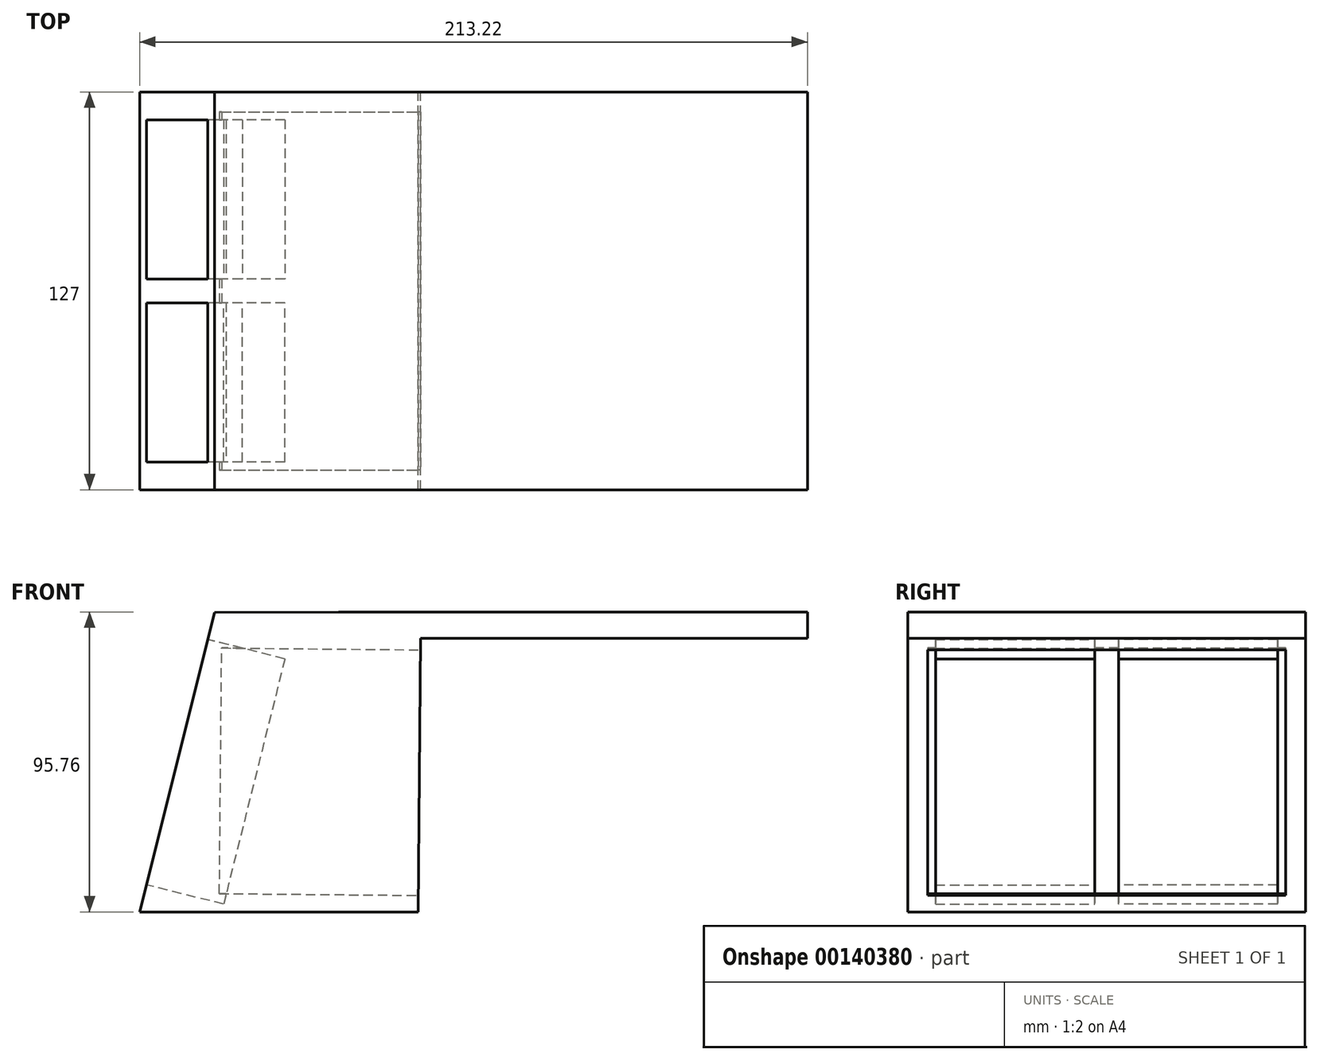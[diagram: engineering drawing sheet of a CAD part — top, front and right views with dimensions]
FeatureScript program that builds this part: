
annotation { "Feature Type Name" : "Feature", "Feature Type Description" : "" }
export const myFeature = defineFeature(function(context is Context, id is Id, definition is map)
    precondition{}
    {
        {
            var Q0;
            Q0=qCreatedBy(makeId("Front.planeOp"),FACE);
            var sketch = newSketch(context, id + "F0", { "sketchPlane" : qUnion([Q0])});
            skLineSegment(sketch, "E0", {"start": v(0, 59) * mm, "end": v(-23.89, -36.55) * mm});
            skLineSegment(sketch, "E1", {"start": v(-23.89, -36.55) * mm, "end": v(65.01, -36.55) * mm});
            skLineSegment(sketch, "E2", {"start": v(39.61, 59.21) * mm, "end": v(0, 59) * mm});
            skLineSegment(sketch, "E3", {"start": v(39.61, 59.21) * mm, "end": v(189.33, 59.21) * mm});
            skLineSegment(sketch, "E4", {"start": v(189.33, 59.21) * mm, "end": v(189.33, 50.73) * mm});
            skLineSegment(sketch, "E5", {"start": v(189.33, 50.73) * mm, "end": v(65.82, 50.73) * mm});
            skLineSegment(sketch, "E6", {"start": v(65.82, 50.73) * mm, "end": v(65.01, -36.55) * mm});
            skSolve(sketch);
        }
        {
            var Q0;
            Q0 = qSketchRegion(id + "F0", true);
            extrude(context, id + "F1", {"entities" : qUnion([Q0]), "depth" : 127 * mm});
        }
        {
            var Q0;
            Q0=makeQuery(id+"F1.opExtrude","SWEPT_FACE",FACE,{"disambiguationData":[OSD([sQuery(id+"F0.wireOp",EDGE,"E6")])]});
            var sketch = newSketch(context, id + "F2", { "sketchPlane" : qUnion([Q0])});
            skPoint(sketch, "E7", {"position": v(-63.5, 8.5) * mm});
            skLineSegment(sketch, "E8.bottom", {"start": v(-6.35, 47.7) * mm, "end": v(-120.65, 47.7) * mm});
            skLineSegment(sketch, "E8.top", {"start": v(-6.35, -30.7) * mm, "end": v(-120.65, -30.7) * mm});
            skLineSegment(sketch, "E8.left", {"start": v(-6.35, 47.7) * mm, "end": v(-6.35, -30.7) * mm});
            skLineSegment(sketch, "E8.right", {"start": v(-120.65, 47.7) * mm, "end": v(-120.65, -30.7) * mm});
            skSolve(sketch);
        }
        {
            var Q0;
            Q0 = qSketchRegion(id + "F2", true);
            extrude(context, id + "F3", {"entities" : qUnion([Q0]), "operationType" : NewBodyOperationType.REMOVE, "oppositeDirection" : true, "depth" : 63.5 * mm});
        }
        {
            var Q0;
            Q0=makeQuery(id+"F1.opExtrude","SWEPT_FACE",FACE,{"disambiguationData":[OSD([sQuery(id+"F0.wireOp",EDGE,"E0")])]});
            var sketch = newSketch(context, id + "F4", { "sketchPlane" : qUnion([Q0])});
            skLineSegment(sketch, "E9.bottom", {"start": v(8.89, 48.36) * mm, "end": v(59.69, 48.36) * mm});
            skLineSegment(sketch, "E9.top", {"start": v(8.9, -32.36) * mm, "end": v(59.7, -32.36) * mm});
            skLineSegment(sketch, "E9.left", {"start": v(8.89, 48.36) * mm, "end": v(8.9, -32.36) * mm});
            skLineSegment(sketch, "E9.right", {"start": v(59.69, 48.36) * mm, "end": v(59.7, -32.36) * mm});
            skLineSegment(sketch, "E10.direction1", {"start": v(8.9, -32.36) * mm, "end": v(63.5, -32.36) * mm, "construction": true});
            skLineSegment(sketch, "E11.bottom", {"start": v(118.11, 48.36) * mm, "end": v(67.3, 48.36) * mm});
            skLineSegment(sketch, "E11.top", {"start": v(118.11, -32.36) * mm, "end": v(67.31, -32.36) * mm});
            skLineSegment(sketch, "E11.left", {"start": v(118.11, 48.36) * mm, "end": v(118.11, -32.36) * mm});
            skLineSegment(sketch, "E11.right", {"start": v(67.3, 48.36) * mm, "end": v(67.31, -32.36) * mm});
            skSolve(sketch);
        }
        {
            var Q0;
            Q0 = qSketchRegion(id + "F4", true);
            extrude(context, id + "F5", {"entities" : qUnion([Q0]), "operationType" : NewBodyOperationType.REMOVE, "oppositeDirection" : true, "depth" : 25.4 * mm});
        }
        {
            var Q0;
            Q0 = qSketchRegion(id + "F4", true);
            extrude(context, id + "F6", {"entities" : qUnion([Q0]), "oppositeDirection" : true, "depth" : 25.4 * mm});
        }
    });
